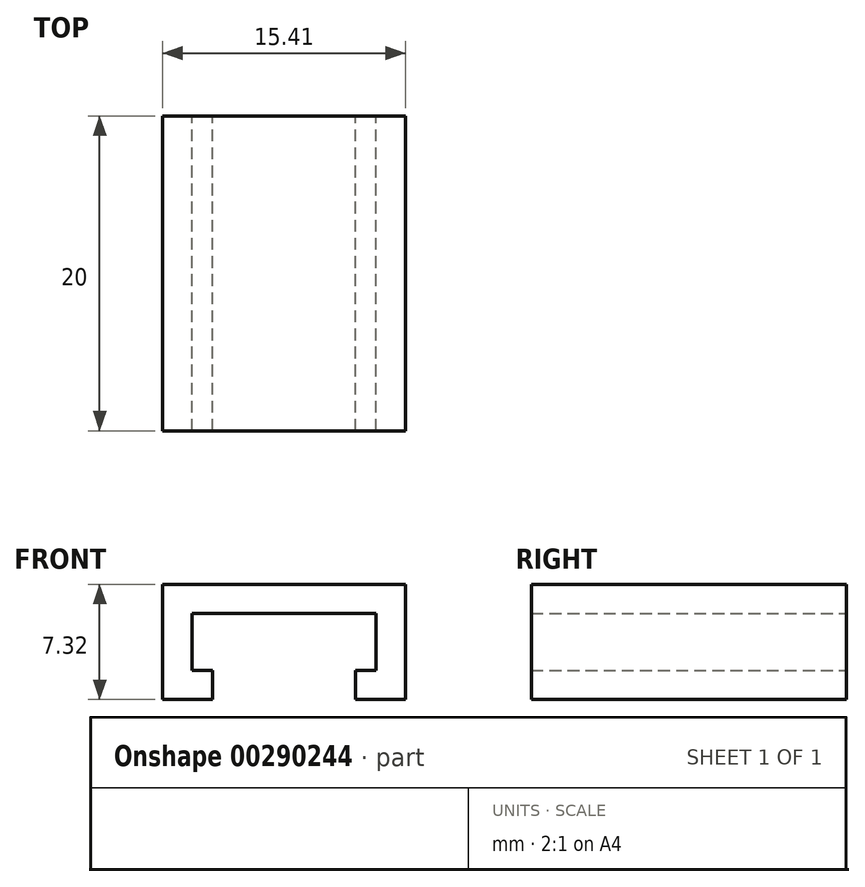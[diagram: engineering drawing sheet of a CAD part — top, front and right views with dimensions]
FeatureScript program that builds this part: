
annotation { "Feature Type Name" : "Feature", "Feature Type Description" : "" }
export const myFeature = defineFeature(function(context is Context, id is Id, definition is map)
    precondition{}
    {
        {
            var Q0;
            Q0=qCreatedBy(makeId("Front.planeOp"),FACE);
            var sketch = newSketch(context, id + "F0", { "sketchPlane" : qUnion([Q0])});
            skLineSegment(sketch, "E0", {"start": v(-10.92, 7.57) * mm, "end": v(0.79, 7.57) * mm});
            skLineSegment(sketch, "E1", {"start": v(0.79, 7.57) * mm, "end": v(0.79, 3.95) * mm});
            skLineSegment(sketch, "E2", {"start": v(0.79, 3.95) * mm, "end": v(-0.53, 3.95) * mm});
            skLineSegment(sketch, "E3", {"start": v(-10.92, 7.57) * mm, "end": v(-10.92, 3.95) * mm});
            skLineSegment(sketch, "E4", {"start": v(-10.92, 3.95) * mm, "end": v(-9.6, 3.95) * mm});
            skLineSegment(sketch, "E5", {"start": v(-9.6, 3.95) * mm, "end": v(-9.6, 2.1) * mm});
            skLineSegment(sketch, "E6", {"start": v(-0.53, 3.95) * mm, "end": v(-0.53, 2.1) * mm});
            skLineSegment(sketch, "E7.0", {"start": v(-12.77, 2.1) * mm, "end": v(-9.6, 2.1) * mm});
            skLineSegment(sketch, "E7.1", {"start": v(2.64, 2.1) * mm, "end": v(1.32, 2.1) * mm});
            skLineSegment(sketch, "E7.2", {"start": v(2.64, 9.42) * mm, "end": v(2.64, 2.1) * mm});
            skLineSegment(sketch, "E7.3", {"start": v(-12.77, 9.42) * mm, "end": v(2.64, 9.42) * mm});
            skLineSegment(sketch, "E7.4", {"start": v(-12.77, 9.42) * mm, "end": v(-12.77, 2.1) * mm});
            skLineSegment(sketch, "E8", {"start": v(1.32, 2.1) * mm, "end": v(-0.53, 2.1) * mm});
            skSolve(sketch);
        }
        {
            var Q0;
            Q0=makeQuery(id+"F0.imprint","IMPRINT",FACE,{"disambiguationData":[TD([[makeQuery(id+"F0.imprint","IMPRINT",EDGE,{"derivedFrom":sQuery(id+"F0.wireOp",EDGE,"E0")}),1.0]])]});
            extrude(context, id + "F1", {"entities" : qUnion([Q0]), "depth" : 20 * mm});
        }
    });
